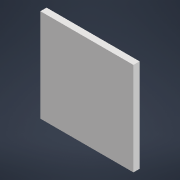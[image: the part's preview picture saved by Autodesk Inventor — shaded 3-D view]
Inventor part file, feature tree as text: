
AUTODESK INVENTOR PART (.ipt)
format: ipt  version: 2022 (Build 260153070, 153G)  size: 84,992 bytes
history: native  units: mm
features: other x1, extrude x1, sketch x1
ambient origin geometry x8: Origin, YZ Plane, XZ Plane, XY Plane, X Axis, Y Axis, Z Axis, Center Point
bodies: Body1 (feature_tree)
feature tree (3):
  other  "Твердое тело1"
  extrude  "Выдавливание1"  Depth=60.0mm
  sketch  "Эскиз1"
